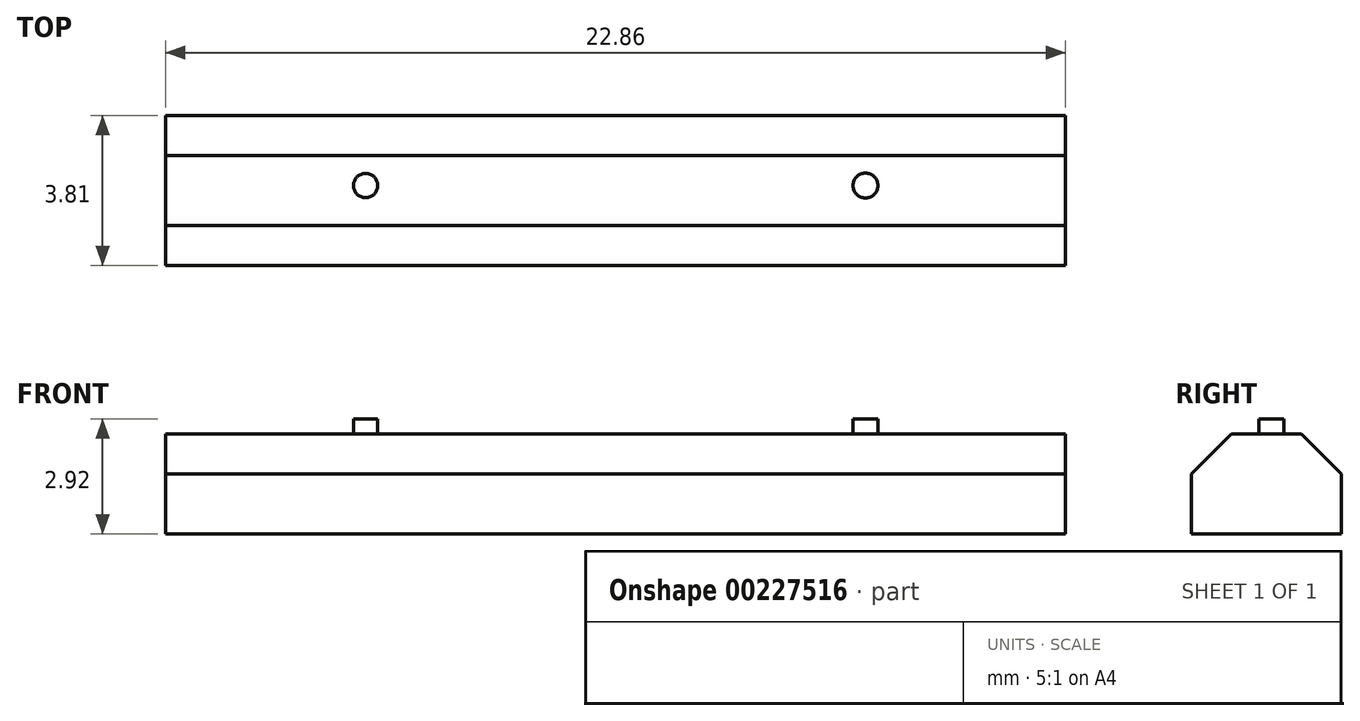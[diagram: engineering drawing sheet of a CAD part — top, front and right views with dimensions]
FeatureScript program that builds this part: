
annotation { "Feature Type Name" : "Feature", "Feature Type Description" : "" }
export const myFeature = defineFeature(function(context is Context, id is Id, definition is map)
    precondition{}
    {
        {
            var Q0;
            Q0=qCreatedBy(makeId("Right.planeOp"),FACE);
            var sketch = newSketch(context, id + "F0", { "sketchPlane" : qUnion([Q0])});
            skLineSegment(sketch, "E0.bottom", {"start": v(0, 0) * mm, "end": v(3.81, 0) * mm});
            skLineSegment(sketch, "E0.top", {"start": v(0, 2.54) * mm, "end": v(3.8, 2.54) * mm});
            skLineSegment(sketch, "E0.left", {"start": v(0, 0) * mm, "end": v(0, 2.54) * mm});
            skLineSegment(sketch, "E0.right", {"start": v(3.81, 0) * mm, "end": v(3.81, 2.54) * mm});
            skSolve(sketch);
        }
        {
            var Q0;
            Q0 = qSketchRegion(id + "F0", true);
            extrude(context, id + "F1", {"entities" : qUnion([Q0]), "depth" : 22.86 * mm});
        }
        {
            var Q0;
            Q0=makeQuery(id+"F1.opExtrude","SWEPT_EDGE",EDGE,{"disambiguationData":[OSD([sQuery(id+"F0.wireOp",EDGE,"E0.top"),sQuery(id+"F0.wireOp",EDGE,"E0.left")])]});
            var Q1;
            Q1=makeQuery(id+"F1.opExtrude","SWEPT_EDGE",EDGE,{"disambiguationData":[OSD([sQuery(id+"F0.wireOp",EDGE,"E0.top"),sQuery(id+"F0.wireOp",EDGE,"E0.right")])]});
            chamfer(context, id + "F2", {"entities" : qUnion([Q0, Q1]), "width" : 1.02 * mm, "tangentPropagation" : true});
        }
        {
            var Q0;
            Q0=makeQuery(id+"F1.opExtrude","SWEPT_FACE",FACE,{"disambiguationData":[OSD([sQuery(id+"F0.wireOp",EDGE,"E0.top")])]});
            var sketch = newSketch(context, id + "F3", { "sketchPlane" : qUnion([Q0])});
            skCircle(sketch, "E1", {"center": v(5.08, 2.03) * mm, "radius": 0.3 * mm});
            skCircle(sketch, "E2", {"center": v(17.78, 2.03) * mm, "radius": 0.32 * mm});
            skSolve(sketch);
        }
        {
            var Q0;
            Q0 = qSketchRegion(id + "F3", true);
            extrude(context, id + "F4", {"entities" : qUnion([Q0]), "operationType" : NewBodyOperationType.ADD, "depth" : 0.38 * mm});
        }
    });
